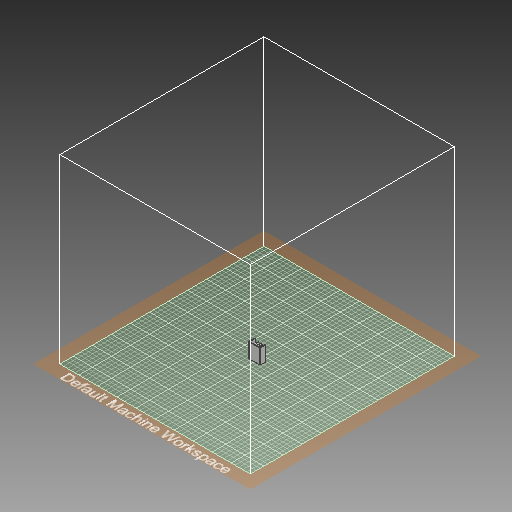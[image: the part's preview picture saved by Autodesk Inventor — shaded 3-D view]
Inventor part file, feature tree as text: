
AUTODESK INVENTOR PART (.ipt)
format: ipt  version: 2019.3 (Build 233278000, 278)  size: 1,131,520 bytes
history: native  units: mm
features: extrude x4, sketch x4, mirror x1, other x1, projected_geometry x1
ambient origin geometry x8: Origin, YZ Plane, XZ Plane, XY Plane, X Axis, Y Axis, Z Axis, Center Point
bodies: Body1 (feature_tree)
feature tree (11):
  extrude  "Extrusion2"  Depth=0.5mm
  extrude  "Extrusion4"  Depth=0.5mm
  mirror  "Mirror1"
  extrude  "Extrusion5"  Depth=0.5mm
  extrude  "Extrusion6"  Depth=1.0mm TaperAngle=360.0deg
  sketch  "Sketch5"  dims[d9=30.0deg d10=400.0mm d12=360.0deg d14=10.0mm d15=0.0mm d16=0.15mm d17=15.0mm d20=22.68928mm d21=2.0mm d22=2.0mm d23=10.0mm d24=10.0mm d25=2.0mm d26=4.0mm d27=2.0mm d28=1.0mm d29=1.0mm d30=1.0mm d31=1.0mm d32=11.0mm d34=10.0mm d35=0.0mm d36=3.0mm d37=0.0mm d38=1.0mm d39=0.0mm]
  other  "Work Axis1"
  sketch  "Sketch2"  dims[d3=5.047545mm d4=0.5mm]
  projected_geometry  "Projected Loop1"
  sketch  "Sketch3"  dims[d5=0.5mm d6=0.5mm]
  sketch  "Sketch4"  dims[d7=60.0deg d8=0.5mm]
